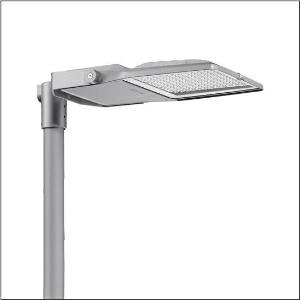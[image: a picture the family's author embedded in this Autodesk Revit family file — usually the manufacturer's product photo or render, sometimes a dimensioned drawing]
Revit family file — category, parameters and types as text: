
# Revit family: floodlight_fl_21_iq_midi___pl61_5xa7782f4c3a_0871
name_source: partatom
category: Lighting Fixtures
units: mm (PartAtom-declared; Revit-internal decimal feet)

## family parameters
Cut with Voids When Loaded = No
Host = Face
Light Source = No
Part Type = Normal
Room Calculation Point = No
Round Connector Dimension = Use Diameter
Shared = No

## types (1)
- --- (1 x LED, 36650 lm, 270.2 W, 4000K)
    Apparent Load = 270 VA
    CIE Flux Codes = 33 65 98 100 100
    Color Rendering = 70
    Color Temperature = 4000K
    Default Elevation = 1800 mm
    Description = Floodlight FL 21 iQ midi, floodlight, primary light control with lens, of PMMA, primary optical cover: protective disc, of toughened safety glass, transparent, light distribution: PL61, light emission: direct distribution, installation type: surface-mounted, LED, High Power LED, rated luminous flux: 36.650lm, luminous efficacy: 136lm/W, light colour: 740, colour temperature: 4000K, control gear: ECG iQ, control: optimised constant luminous flux control (CLO 2.0), Desk-Remote (wireless, voltage-free reading and setting of iQ features in the workshop via application-optimized NFC function/RFID function), Smart-Wire, Night-Set, Temp-Guard, Auto-Match, Street-Remote, with terminal, 6-pole, mains connection: 220..240V, AC, 50/60Hz, start of lifetime: 270W, end of service life: 287W, reduction: 118W, luminaire housing, of diecast aluminium, powder-coated, Siteco® metallic grey (DB 702S), corrosivity category C5 mid according to DIN EN ISO 12944, sealing non-destructively replaceable, please order mast flange separately, mast bracket, of steel, galvanised, powder-coated, Siteco® metallic grey (DB 702S), protection rating (complete): IP66, insulation class (complete): insulation class II (safety insulation), certification: CE, ENEC, VDE, protection symbol: D, impact resistance: IK08, permissible operating ambient temperature: -40..+40°C, permissible operating ambient temperature for outdoor applications: -40..+50°C, standard: DIN EN 12944, LABS conformity tested according to VDMA 24364:2018-05, packaging unit: 1 piece

Light Distribution: PL61
    Height = 76 mm
    Lamp = 1 x LED
    Lamp Light Flux = 36650 lm
    Lamp Power = 270.2 W
    Lamp count = 1
    Length = 657 mm
    Luminous efficacy = 136 lm/W
    Manufacturer = Siteco
    ModVariant = No
    Model = 5XA7782F4C3A
    Number of Poles = 1
    OnlyDefault = Yes
    Power Factor = 1
    Product Name = Floodlight FL 21 iQ midi | PL61
    Product group = floodlight | pylon annexe
    ProductGroupID = 6200
    Protection Class = Protection class II
    Protection Degree = IP 66
    RLX_Detail_Level = 1
    RLX_Emergency_Light_Flux = 0 lm
    RLX_Emergency_Type = 0
    RLX_Emergency_Type_DB = No
    RlxData = <blob elided: 153621 chars, md5=d8cb2da6>
    Socket = socket
    Standby Power = 0 W
    System Light Flux = 36650 lm
    System Power = 270 W
    Type Comments = factory setting: luminous flux: 100 % | dim-lin: 254 | 620 mA
    Type Image = l_1007123.jpg
    URL = http://relux.com
    VarID = @adj_077031
    Voltage = 0 V
    Weight = 0.00 kg
    Width = 442 mm

## geometry (parser evidence)
native form markers: Blend x4, Sweep x14
no freeform markers — native parametric forms only
